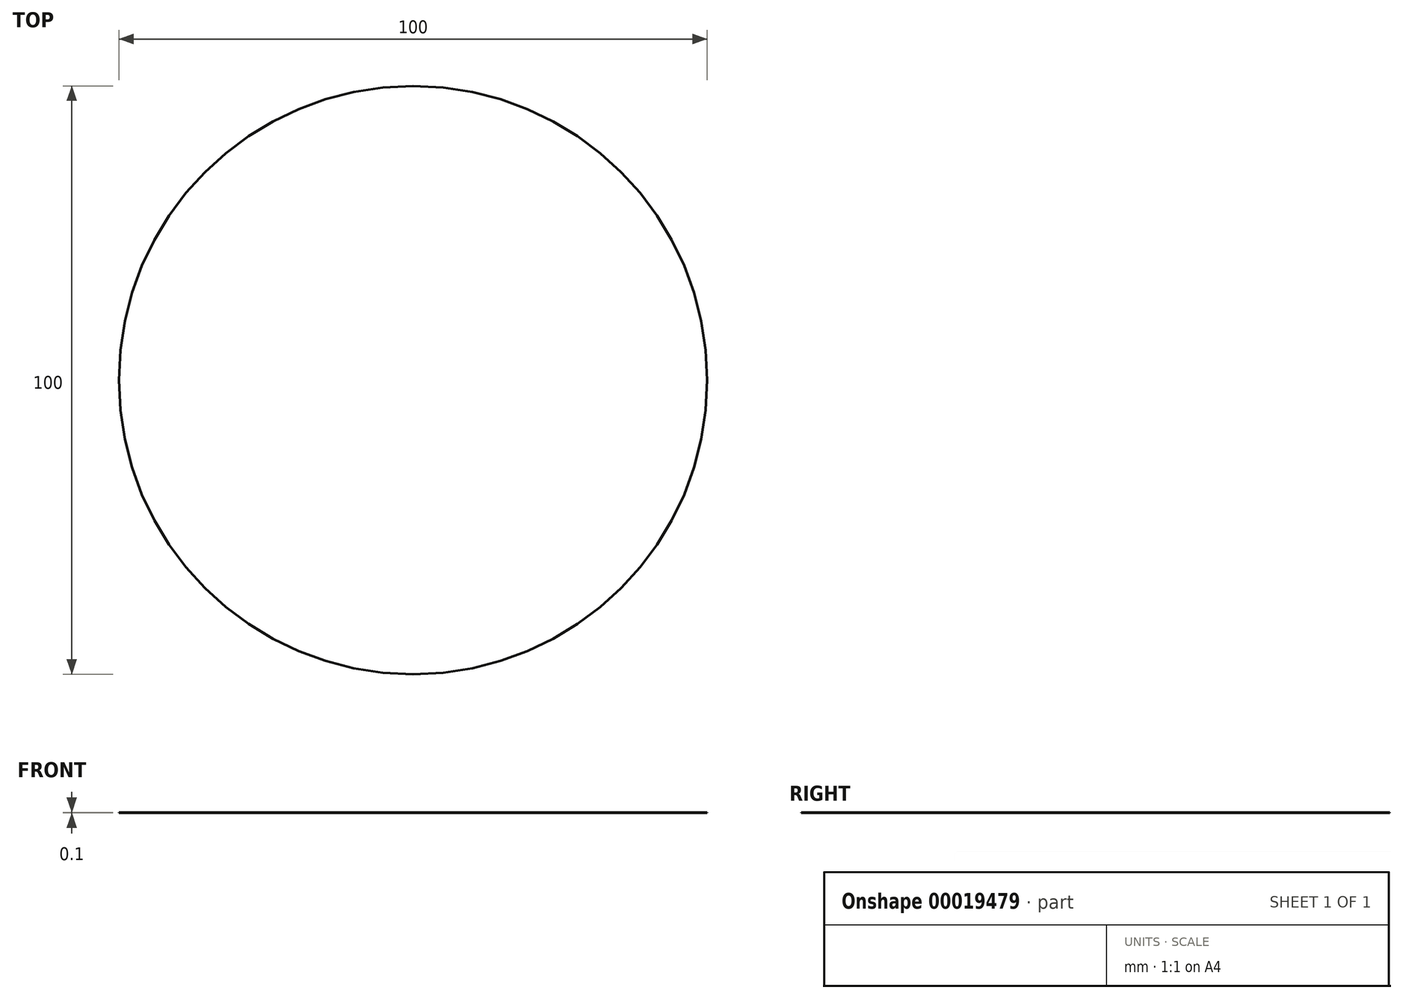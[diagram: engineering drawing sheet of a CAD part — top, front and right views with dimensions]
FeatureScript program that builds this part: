
annotation { "Feature Type Name" : "Feature", "Feature Type Description" : "" }
export const myFeature = defineFeature(function(context is Context, id is Id, definition is map)
    precondition{}
    {
        {
            var Q0;
            Q0=qCreatedBy(makeId("Top.planeOp"),FACE);
            var sketch = newSketch(context, id + "F0", { "sketchPlane" : qUnion([Q0])});
            skCircle(sketch, "E0", {"center": v(0, 0) * mm, "radius": 50 * mm});
            skSolve(sketch);
        }
        {
            var Q0;
            Q0=makeQuery(id+"F0.imprint","IMPRINT",FACE,{"disambiguationData":[TD([[makeQuery(id+"F0.imprint","IMPRINT",EDGE,{"derivedFrom":sQuery(id+"F0.wireOp",EDGE,"E0")}),1.0]])]});
            extrude(context, id + "F1", {"entities" : qUnion([Q0]), "depth" : 0.1 * mm});
        }
    });
